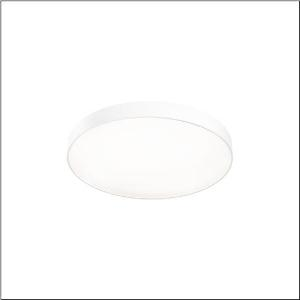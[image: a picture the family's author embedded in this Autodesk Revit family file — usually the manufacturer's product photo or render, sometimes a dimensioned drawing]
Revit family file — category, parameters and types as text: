
# Revit family: round_21_m_51mr36fm8421w
name_source: partatom
category: Lighting Fixtures
units: mm (PartAtom-declared; Revit-internal decimal feet)

## family parameters
Cut with Voids When Loaded = No
Host = Face
Light Source = No
Part Type = Normal
Room Calculation Point = No
Round Connector Dimension = Use Diameter
Shared = No

## types (1)
- --- (1 x LED, 8140 lm, 61.1 W, 4000K)
    Apparent Load = 61 VA
    CIE Flux Codes = 49 80 96 100 100
    Color Rendering = 80
    Color Temperature = 4000K
    Default Elevation = 1800 mm
    Description = Round 21 M, wall and ceiling luminaire, primary optical cover: cover, of PMMA, opal, light emission: direct distribution, primary light characteristic: symmetric, installation type: surface-mounted, suspended mounting, LED, rated luminous flux: 8.140lm, luminous efficacy: 133lm/W, light colour: 840, colour temperature: 4000K, with terminal, 3-pole, mains connection: 230V, AC, 50/60Hz, rated input power: 61W, housing, of aluminium, coated, white, diameter: 600mm, height: 62mm, protection rating (complete): IP40, insulation class (complete): insulation class I (protective earthing), certification: CE, impact resistance: IK04, permissible operating ambient temperature: -10..+35°C, packaging unit: 1 piece
    Height = 87 mm
    Lamp = 1 x LED
    Lamp Light Flux = 8140 lm
    Lamp Power = 61.1 W
    Lamp count = 1
    Length = 600 mm
    Luminous efficacy = 133 lm/W
    Manufacturer = Siteco
    ModVariant = No
    Model = 51MR36FM8421W
    Mounting Place = Ceiling
    Mounting Type = Surface mounted
    Number of Poles = 1
    OnlyDefault = Yes
    Power Factor = 1
    Product Name = Round 21 M
    Product group = wall and ceiling luminaire
    ProductGroupID = 302
    Protection Class = Protection class I
    Protection Degree = IP 40
    RLX_Detail_Level = 1
    RLX_Emergency_Light_Flux = 0 lm
    RLX_Emergency_Type = 0
    RLX_Emergency_Type_DB = No
    RlxData = <blob elided: 14301 chars, md5=a1459d76>
    Socket = socket
    Standby Power = 0 W
    System Light Flux = 8140 lm
    System Power = 61 W
    Type Comments = factory setting: luminous flux: 100 % | (ON | ON | ON | ON) | 700 mA
    Type Image = l_1258330.jpg
    URL = http://relux.com
    VarID = @adj_032079
    Voltage = 0 V
    Weight = 0.00 kg
    Width = 0 mm  [stored 0 ft]

note: [stored X ft] marks values corroborated as IEEE doubles in the binary element streams (Revit-internal decimal feet)

## geometry (parser evidence)
native form markers: Sweep x12
no freeform markers — native parametric forms only
